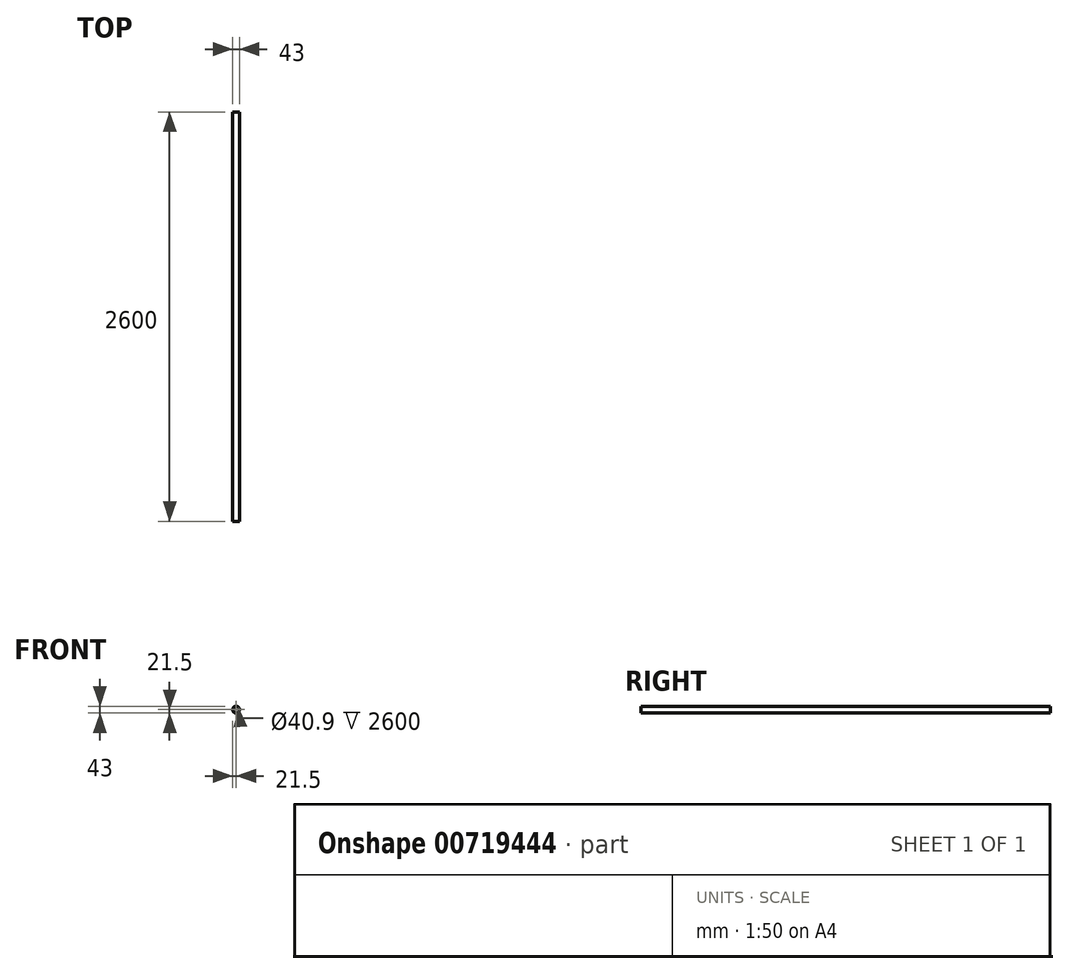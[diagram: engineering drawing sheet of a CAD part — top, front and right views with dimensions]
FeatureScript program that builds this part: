
annotation { "Feature Type Name" : "Feature", "Feature Type Description" : "" }
export const myFeature = defineFeature(function(context is Context, id is Id, definition is map)
    precondition{}
    {
        {
            var Q0;
            Q0=qCreatedBy(makeId("Front.planeOp"),FACE);
            var sketch = newSketch(context, id + "F0", { "sketchPlane" : qUnion([Q0])});
            skCircle(sketch, "E0", {"center": v(0, 0) * mm, "radius": 20.45 * mm});
            skCircle(sketch, "E1", {"center": v(0, 0) * mm, "radius": 21.5 * mm});
            skSolve(sketch);
        }
        {
            var Q0;
            Q0=makeQuery(id+"F0.imprint","IMPRINT",FACE,{"disambiguationData":[TD([[makeQuery(id+"F0.imprint","IMPRINT",EDGE,{"derivedFrom":sQuery(id+"F0.wireOp",EDGE,"E0")}),-1.0]])]});
            extrude(context, id + "F1", {"entities" : qUnion([Q0]), "depth" : 2600 * mm, "offsetDistance" : 25 * mm});
        }
    });
